# Revit family: Roofing-Aquaknight-Butynol_Dropper_DN80
name_source: partatom
category: Plumbing Fixtures
revit_build: Autodesk Revit 2016 (Build: 20150714_1515(x64)
units: mm (PartAtom-declared; Revit-internal decimal feet)

## family parameters
Always vertical = Yes
Cut with Voids When Loaded = No
OmniClass Number = 23.60.30.11
OmniClass Title = Pipework Products for General Use
Part Type = Normal
Room Calculation Point = No
Round Connector Dimension = Use Diameter
Shared = No
Work Plane-Based = No

## types (1)
- DN80
    250mm Head Flow = 0.0 L/s
    400mm Head Flow = 0.0 L/s
    Connector Diameter = 74 mm  [stored 0.242782 ft]
    DN = 80
    Depth = 204 mm  [stored 0.669291 ft]
    Description = Butynol Dropper 300x80
    Drain Diameter = 73.5 mm  [stored 0.241142 ft]
    Drain Interior Diameter = 68.5 mm  [stored 0.224738 ft]
    Drain Interior Radius = 34.25 mm  [stored 0.112369 ft]
    Drain Radius = 36.75 mm  [stored 0.120571 ft]
    Extrusion End = 2.5 mm  [stored 0.0082021 ft]
    Length = 298 mm  [stored 0.97769 ft]
    Manufacturer = Aquaknight Industries Ltd
    Max Weir Flow = 5.0 L/s
    Model = 2100.107
    Pipe Joint Location = 149 mm  [stored 0.488845 ft]
    URL = www.aquaknight.co.nz
    Width = 204 mm  [stored 0.669291 ft]

note: [stored X ft] marks values corroborated as IEEE doubles in the binary element streams (Revit-internal decimal feet)

## geometry (parser evidence)
native form markers: Extrusion x1, Sweep x3
no freeform markers — native parametric forms only
